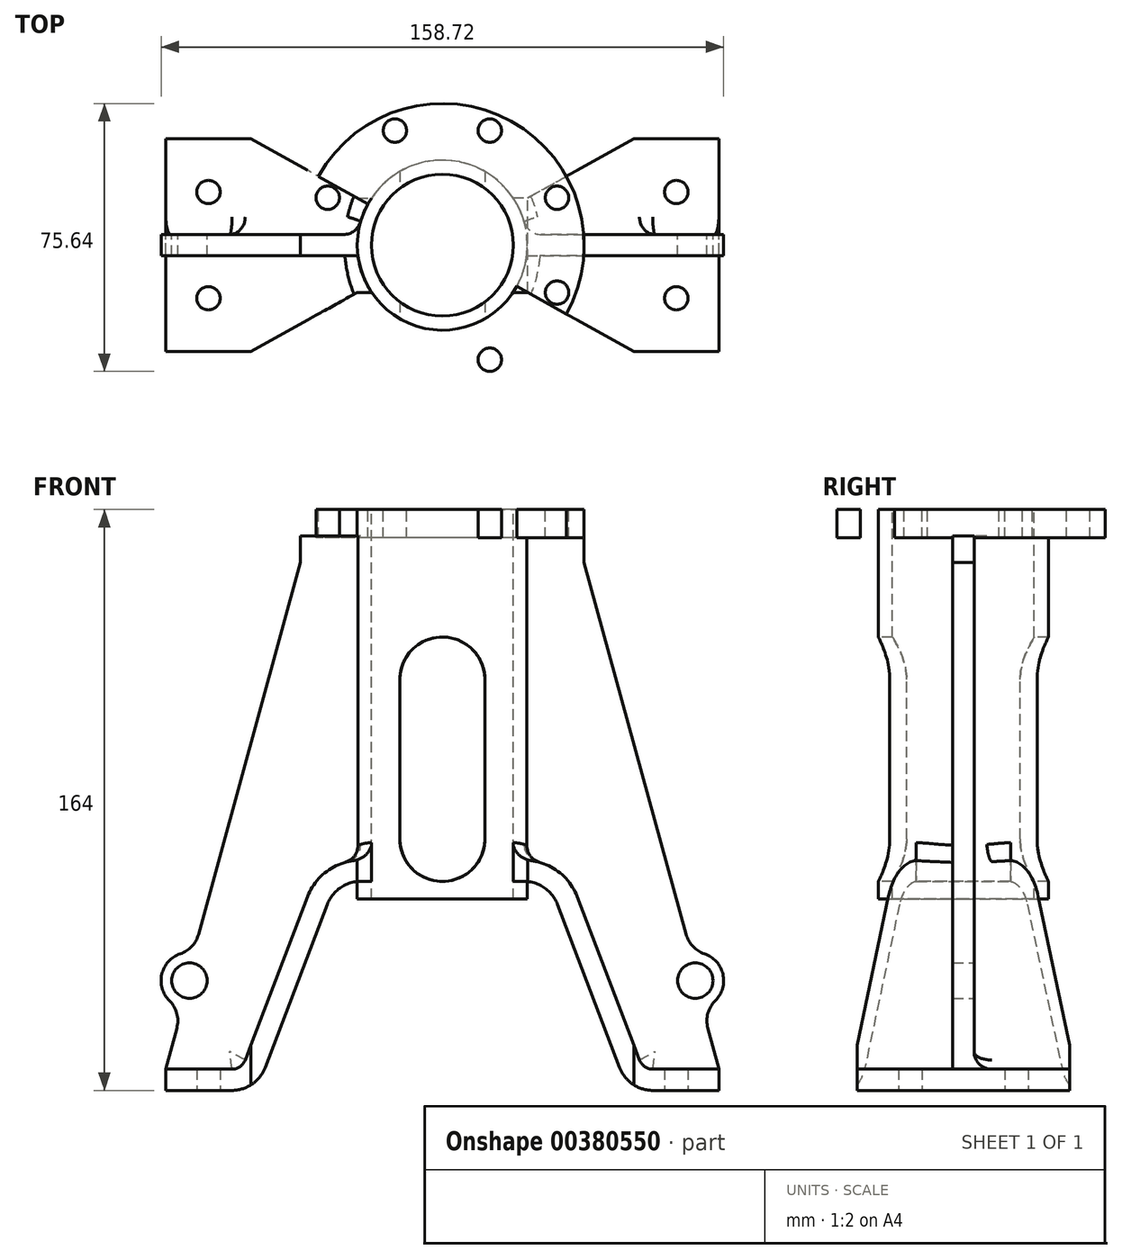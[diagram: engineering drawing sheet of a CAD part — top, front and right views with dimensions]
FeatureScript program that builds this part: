
annotation { "Feature Type Name" : "Feature", "Feature Type Description" : "" }
export const myFeature = defineFeature(function(context is Context, id is Id, definition is map)
    precondition{}
    {
        {
            var Q0;
            Q0=qCreatedBy(makeId("Top.planeOp"),FACE);
            var sketch = newSketch(context, id + "F0", { "sketchPlane" : qUnion([Q0])});
            skLineSegment(sketch, "E0", {"start": v(0, 47.18) * mm, "end": v(0, -47.18) * mm, "construction": true});
            skCircle(sketch, "E1", {"center": v(0, 0) * mm, "radius": 40 * mm});
            skLineSegment(sketch, "E2", {"start": v(-78, 0) * mm, "end": v(78, 0) * mm, "construction": true});
            skLineSegment(sketch, "E3.bottom", {"start": v(78, -3) * mm, "end": v(39.89, -3) * mm});
            skLineSegment(sketch, "E3.top", {"start": v(78, 3) * mm, "end": v(39.89, 3) * mm});
            skLineSegment(sketch, "E3.left", {"start": v(78, -3) * mm, "end": v(78, 3) * mm});
            skLineSegment(sketch, "E3.right", {"start": v(-78, -3) * mm, "end": v(-78, 3) * mm});
            skLineSegment(sketch, "E4.trimOffspring", {"start": v(-39.89, 3) * mm, "end": v(-78, 3) * mm});
            skLineSegment(sketch, "E5.trimOffspring", {"start": v(-39.89, -3) * mm, "end": v(-78, -3) * mm});
            skLineSegment(sketch, "E6", {"start": v(9.18, 22.17) * mm, "end": v(23.37, 56.42) * mm, "construction": true});
            skLineSegment(sketch, "E7", {"start": v(22.17, 9.18) * mm, "end": v(61.04, 25.28) * mm, "construction": true});
            skCircle(sketch, "E8", {"center": v(0, 0) * mm, "radius": 35 * mm, "construction": true});
            skCircle(sketch, "E9", {"center": v(13.4, 32.34) * mm, "radius": 3.3 * mm});
            skCircle(sketch, "E10", {"center": v(32.34, 13.4) * mm, "radius": 3.3 * mm});
            skLineSegment(sketch, "E11", {"start": v(78, -30) * mm, "end": v(78, 30) * mm});
            skLineSegment(sketch, "E12", {"start": v(78, 30) * mm, "end": v(54, 30) * mm});
            skLineSegment(sketch, "E13", {"start": v(20.98, 11.66) * mm, "end": v(54, 30) * mm});
            skCircle(sketch, "E14", {"center": v(66, 15) * mm, "radius": 3.3 * mm});
            skCircle(sketch, "E15.MirrorC", {"center": v(66, -15) * mm, "radius": 3.3 * mm});
            skLineSegment(sketch, "E16.MirrorCS", {"start": v(78, -30) * mm, "end": v(54, -30) * mm});
            skLineSegment(sketch, "E17.MirrorCS", {"start": v(20.98, -11.66) * mm, "end": v(54, -30) * mm});
            skCircle(sketch, "E18.MirrorC", {"center": v(32.34, -13.4) * mm, "radius": 3.3 * mm});
            skCircle(sketch, "E19.MirrorC", {"center": v(13.4, -32.34) * mm, "radius": 3.3 * mm});
            skLineSegment(sketch, "E20", {"start": v(66, 15) * mm, "end": v(66, 30) * mm, "construction": true});
            skLineSegment(sketch, "E21", {"start": v(66, 15) * mm, "end": v(78, 15) * mm, "construction": true});
            skCircle(sketch, "E22.MirrorC", {"center": v(-13.4, 32.34) * mm, "radius": 3.3 * mm});
            skCircle(sketch, "E23.MirrorC", {"center": v(-32.34, 13.4) * mm, "radius": 3.3 * mm});
            skCircle(sketch, "E24.MirrorC", {"center": v(-32.34, -13.4) * mm, "radius": 3.3 * mm});
            skCircle(sketch, "E25.MirrorC", {"center": v(-13.4, -32.34) * mm, "radius": 3.3 * mm});
            skCircle(sketch, "E26.MirrorC", {"center": v(-66, -15) * mm, "radius": 3.3 * mm});
            skLineSegment(sketch, "E27.MirrorCS", {"start": v(-78, -30) * mm, "end": v(-54, -30) * mm});
            skLineSegment(sketch, "E28.MirrorCS", {"start": v(-78, -30) * mm, "end": v(-78, 30) * mm});
            skLineSegment(sketch, "E29.MirrorCS", {"start": v(-78, 30) * mm, "end": v(-54, 30) * mm});
            skLineSegment(sketch, "E30.MirrorCS", {"start": v(-20.98, 11.66) * mm, "end": v(-54, 30) * mm});
            skLineSegment(sketch, "E31.MirrorCS", {"start": v(-20.98, -11.66) * mm, "end": v(-54, -30) * mm});
            skCircle(sketch, "E32.MirrorC", {"center": v(-66, 15) * mm, "radius": 3.3 * mm});
            skCircle(sketch, "E33", {"center": v(0, 0) * mm, "radius": 24 * mm});
            skCircle(sketch, "E34", {"center": v(0, 0) * mm, "radius": 20 * mm});
            skSolve(sketch);
        }
        {
            var Q0;
            Q0=makeQuery(id+"F0.imprint","IMPRINT",FACE,{"disambiguationData":[TD([[makeQuery(id+"F0.imprint","IMPRINT",EDGE,{"derivedFrom":sQuery(id+"F0.wireOp",EDGE,"E9")}),-1.0]])]});
            var Q1;
            Q1=makeQuery(id+"F0.imprint","IMPRINT",FACE,{"disambiguationData":[TD([[makeQuery(id+"F0.imprint","IMPRINT",EDGE,{"derivedFrom":sQuery(id+"F0.wireOp",EDGE,"E23.MirrorC")}),1.0]])]});
            var Q2;
            Q2=makeQuery(id+"F0.imprint","IMPRINT",FACE,{"disambiguationData":[TD([[makeQuery(id+"F0.imprint","IMPRINT",EDGE,{"derivedFrom":sQuery(id+"F0.wireOp",EDGE,"E19.MirrorC")}),1.0]])]});
            var Q3;
            Q3=makeQuery(id+"F0.imprint","IMPRINT",FACE,{"disambiguationData":[TD([[makeQuery(id+"F0.imprint","IMPRINT",EDGE,{"derivedFrom":sQuery(id+"F0.wireOp",EDGE,"E10")}),-1.0]])]});
            extrude(context, id + "F1", {"entities" : qUnion([Q0, Q1, Q2, Q3]), "oppositeDirection" : true, "depth" : 8 * mm});
        }
        {
            var Q0;
            Q0=qCreatedBy(makeId("Front.planeOp"),FACE);
            var sketch = newSketch(context, id + "F2", { "sketchPlane" : qUnion([Q0])});
            skLineSegment(sketch, "E35", {"start": v(40, 0) * mm, "end": v(40, -15) * mm});
            skLineSegment(sketch, "E36", {"start": v(0, 0) * mm, "end": v(0, -164) * mm, "construction": true});
            skLineSegment(sketch, "E37", {"start": v(59.35, -164) * mm, "end": v(78, -164) * mm});
            skLineSegment(sketch, "E38", {"start": v(78, -164) * mm, "end": v(78, -158) * mm});
            skLineSegment(sketch, "E39", {"start": v(78, -158) * mm, "end": v(74.92, -146.4) * mm});
            skLineSegment(sketch, "E40.bottom", {"start": v(-20, 0) * mm, "end": v(20, 0) * mm});
            skLineSegment(sketch, "E40.top", {"start": v(-20, -70.5) * mm, "end": v(20, -70.5) * mm, "construction": true});
            skLineSegment(sketch, "E40.left", {"start": v(-20, 0) * mm, "end": v(-20, -70.5) * mm, "construction": true});
            skLineSegment(sketch, "E40.right", {"start": v(20, 0) * mm, "end": v(20, -70.5) * mm, "construction": true});
            skCircle(sketch, "E41", {"center": v(0, -48) * mm, "radius": 12 * mm, "construction": true});
            skCircle(sketch, "E42", {"center": v(0, -93) * mm, "radius": 12 * mm, "construction": true});
            skPoint(sketch, "E43", {"position": v(0, -70.5) * mm});
            skLineSegment(sketch, "E44", {"start": v(0, -93) * mm, "end": v(-12, -93) * mm, "construction": true});
            skLineSegment(sketch, "E45", {"start": v(-12, -93) * mm, "end": v(-12, -48) * mm});
            skLineSegment(sketch, "E46", {"start": v(-12, -48) * mm, "end": v(12, -48) * mm, "construction": true});
            skLineSegment(sketch, "E47", {"start": v(12, -48) * mm, "end": v(12, -93) * mm});
            skLineSegment(sketch, "E48", {"start": v(12, -93) * mm, "end": v(-12, -93) * mm, "construction": true});
            skArc(sketch, "E49", {"start": v(12, -48) * mm, "mid": v(0, -36) * mm, "end": v(-12, -48) * mm});
            skArc(sketch, "E50", {"start": v(-12, -93) * mm, "mid": v(0, -105) * mm, "end": v(12, -93) * mm});
            skLineSegment(sketch, "E51", {"start": v(20, -70.5) * mm, "end": v(20, -112.54) * mm, "construction": true});
            skLineSegment(sketch, "E52", {"start": v(-20, -112.54) * mm, "end": v(-20, -70.5) * mm, "construction": true});
            skLineSegment(sketch, "E53", {"start": v(0, -105) * mm, "end": v(23.1, -105) * mm, "construction": true});
            skLineSegment(sketch, "E54", {"start": v(30, -105) * mm, "end": v(30, -164) * mm});
            skLineSegment(sketch, "E55", {"start": v(50, -157.56) * mm, "end": v(32.45, -111.44) * mm});
            skLineSegment(sketch, "E56", {"start": v(38.06, -109.3) * mm, "end": v(55.61, -155.42) * mm});
            skLineSegment(sketch, "E57", {"start": v(59.35, -158) * mm, "end": v(78, -158) * mm});
            skPoint(sketch, "E58.visualSharp", {"position": v(30, -105) * mm});
            skArc(sketch, "E58.filletArc", {"start": v(32.45, -111.44) * mm, "mid": v(28.78, -106.77) * mm, "end": v(23.1, -105) * mm});
            skPoint(sketch, "E59.newPointB", {"position": v(-78, -164) * mm});
            skArc(sketch, "E59.filletArc", {"start": v(50, -157.56) * mm, "mid": v(53.67, -162.23) * mm, "end": v(59.35, -164) * mm});
            skPoint(sketch, "E60.visualSharp", {"position": v(33.98, -98.59) * mm});
            skArc(sketch, "E60.filletArc", {"start": v(38.06, -109.3) * mm, "mid": v(32.19, -101.83) * mm, "end": v(23.1, -99) * mm});
            skPoint(sketch, "E61.visualSharp", {"position": v(56.6, -158) * mm});
            skArc(sketch, "E61.filletArc", {"start": v(55.61, -155.42) * mm, "mid": v(57.08, -157.3) * mm, "end": v(59.35, -158) * mm});
            skLineSegment(sketch, "E62.MirrorCS", {"start": v(-50, -157.56) * mm, "end": v(-32.45, -111.44) * mm});
            skLineSegment(sketch, "E63.MirrorCS", {"start": v(-38.06, -109.3) * mm, "end": v(-55.61, -155.42) * mm});
            skArc(sketch, "E64.MirrorCS", {"start": v(-38.06, -109.3) * mm, "mid": v(-32.19, -101.83) * mm, "end": v(-23.1, -99) * mm});
            skArc(sketch, "E65.MirrorCS", {"start": v(-32.45, -111.44) * mm, "mid": v(-28.78, -106.77) * mm, "end": v(-23.1, -105) * mm});
            skLineSegment(sketch, "E66.MirrorCS", {"start": v(-59.35, -158) * mm, "end": v(-78, -158) * mm});
            skArc(sketch, "E67.MirrorCS", {"start": v(-50, -157.56) * mm, "mid": v(-53.67, -162.23) * mm, "end": v(-59.35, -164) * mm});
            skPoint(sketch, "E68.MirrorP", {"position": v(-56.6, -158) * mm});
            skArc(sketch, "E69.MirrorCS", {"start": v(-55.61, -155.42) * mm, "mid": v(-57.08, -157.3) * mm, "end": v(-59.35, -158) * mm});
            skLineSegment(sketch, "E70.MirrorCS", {"start": v(-59.35, -164) * mm, "end": v(-78, -164) * mm});
            skLineSegment(sketch, "E71.MirrorCS", {"start": v(-78, -164) * mm, "end": v(-78, -158) * mm});
            skLineSegment(sketch, "E72.MirrorCS", {"start": v(-40, 0) * mm, "end": v(-40, -15) * mm});
            skLineSegment(sketch, "E73", {"start": v(-23.1, -99) * mm, "end": v(23.1, -99) * mm, "construction": true});
            skLineSegment(sketch, "E74", {"start": v(-23.1, -105) * mm, "end": v(23.1, -105) * mm, "construction": true});
            skCircle(sketch, "E75", {"center": v(71.36, -133) * mm, "radius": 5 * mm});
            skArc(sketch, "E76", {"start": v(77, -138.67) * mm, "mid": v(79.15, -131.2) * mm, "end": v(73.94, -125.43) * mm});
            skLineSegment(sketch, "E77", {"start": v(68.82, -119.98) * mm, "end": v(40, -15) * mm});
            skPoint(sketch, "E78.newPointB", {"position": v(40, -15) * mm});
            skArc(sketch, "E78.filletArc", {"start": v(77, -138.67) * mm, "mid": v(74.92, -142.25) * mm, "end": v(74.92, -146.4) * mm});
            skArc(sketch, "E79.filletArc", {"start": v(68.82, -119.98) * mm, "mid": v(70.7, -123.34) * mm, "end": v(73.94, -125.43) * mm});
            skLineSegment(sketch, "E80.MirrorCS", {"start": v(-68.82, -119.98) * mm, "end": v(-40, -15) * mm});
            skCircle(sketch, "E81.MirrorC", {"center": v(-71.36, -133) * mm, "radius": 5 * mm});
            skArc(sketch, "E82.MirrorCS", {"start": v(-77, -138.67) * mm, "mid": v(-79.15, -131.2) * mm, "end": v(-73.94, -125.43) * mm});
            skArc(sketch, "E83.MirrorCS", {"start": v(-77, -138.67) * mm, "mid": v(-74.92, -142.25) * mm, "end": v(-74.92, -146.4) * mm});
            skArc(sketch, "E84.MirrorCS", {"start": v(-68.82, -119.98) * mm, "mid": v(-70.7, -123.34) * mm, "end": v(-73.94, -125.43) * mm});
            skLineSegment(sketch, "E85.MirrorCS", {"start": v(-78, -158) * mm, "end": v(-74.92, -146.4) * mm});
            skLineSegment(sketch, "E86", {"start": v(-40, -7.5) * mm, "end": v(40, -7.5) * mm});
            skLineSegment(sketch, "E87.bottom", {"start": v(-24.01, 0) * mm, "end": v(24.02, 0) * mm});
            skLineSegment(sketch, "E87.top", {"start": v(-24.01, -112.5) * mm, "end": v(24.02, -112.5) * mm});
            skLineSegment(sketch, "E87.left", {"start": v(-24.01, 0) * mm, "end": v(-24.01, -112.5) * mm});
            skLineSegment(sketch, "E87.right", {"start": v(24.02, 0) * mm, "end": v(24.02, -112.5) * mm});
            skSolve(sketch);
        }
        {
            var Q0;
            Q0=makeQuery(id+"F0.imprint","IMPRINT",FACE,{"disambiguationData":[TD([[makeQuery(id+"F0.imprint","IMPRINT",EDGE,{"derivedFrom":sQuery(id+"F0.wireOp",EDGE,"E33")}),1.0]])]});
            extrude(context, id + "F3", {"entities" : qUnion([Q0]), "operationType" : NewBodyOperationType.ADD, "oppositeDirection" : true, "depth" : 110 * mm});
        }
        {
            var Q0;
            Q0=makeQuery(id+"F2.imprint","IMPRINT",FACE,{"disambiguationData":[TD([[makeQuery(id+"F2.imprint","IMPRINT",EDGE,{"derivedFrom":sQuery(id+"F2.wireOp",EDGE,"E45")}),-1.0]])]});
            extrude(context, id + "F4", {"entities" : qUnion([Q0]), "operationType" : NewBodyOperationType.REMOVE, "oppositeDirection" : true, "depth" : 61.5 * mm, "hasSecondDirection" : true, "secondDirectionOppositeDirection" : false, "secondDirectionDepth" : 75.8 * mm});
        }
        {
            var Q0;
            {var subQ4=sQuery(id+"F2.wireOp",EDGE,"E63.MirrorCS");Q0=makeQuery(id+"F2.imprint","IMPRINT",FACE,{"disambiguationData":[TD([[makeQuery(id+"F2.imprint","IMPRINT",EDGE,{"derivedFrom":subQ4}),-1.0]])]});}
            var Q1;
            Q1=makeQuery(id+"F2.imprint","IMPRINT",FACE,{"disambiguationData":[TD([[makeQuery(id+"F2.imprint","IMPRINT",EDGE,{"derivedFrom":sQuery(id+"F2.wireOp",EDGE,"E39")}),1.0]])]});
            extrude(context, id + "F5", {"entities" : qUnion([Q0, Q1]), "operationType" : NewBodyOperationType.ADD, "depth" : 3 * mm, "hasSecondDirection" : true, "secondDirectionOppositeDirection" : true, "secondDirectionDepth" : 3 * mm});
        }
        {
            var Q0;
            {var subQ1=sQuery(id+"F2.wireOp",EDGE,"E62.MirrorCS");Q0=makeQuery(id+"F2.imprint","IMPRINT",FACE,{"disambiguationData":[TD([[makeQuery(id+"F2.imprint","IMPRINT",EDGE,{"derivedFrom":subQ1}),1.0]])]});}
            var Q1;
            Q1=makeQuery(id+"F2.imprint","IMPRINT",FACE,{"disambiguationData":[TD([[makeQuery(id+"F2.imprint","IMPRINT",EDGE,{"derivedFrom":sQuery(id+"F2.wireOp",EDGE,"E37")}),1.0]])]});
            extrude(context, id + "F6", {"entities" : qUnion([Q0, Q1]), "operationType" : NewBodyOperationType.ADD, "depth" : 30 * mm, "hasSecondDirection" : true, "secondDirectionOppositeDirection" : true, "secondDirectionDepth" : 30 * mm});
        }
        {
            var Q0;
            {var subQ0=sQuery(id+"F2.wireOp",EDGE,"E69.MirrorCS");var subQ1=sQuery(id+"F2.wireOp",EDGE,"E87.left");var subQ2=sQuery(id+"F2.wireOp",EDGE,"E71.MirrorCS");var subQ3=sQuery(id+"F2.wireOp",EDGE,"E66.MirrorCS");var subQ4=sQuery(id+"F2.wireOp",EDGE,"E64.MirrorCS");var subQ5=sQuery(id+"F2.wireOp",EDGE,"E63.MirrorCS");Q0=makeQuery(id+"F6.boolean.opBoolean","SPLIT",FACE,{"disambiguationData":[TD([makeQuery(id+"F6.opExtrude","CAP_FACE",FACE,{"disambiguationData":[OSD([sQuery(id+"F2.wireOp",EDGE,"E62.MirrorCS"),subQ5,subQ4,sQuery(id+"F2.wireOp",EDGE,"E65.MirrorCS"),subQ3,sQuery(id+"F2.wireOp",EDGE,"E67.MirrorCS"),subQ0,sQuery(id+"F2.wireOp",EDGE,"E70.MirrorCS"),subQ2,subQ1])],"isStart":false})])],"derivedFrom":makeQuery(id+"F6.opExtrude","SWEPT_FACE",FACE,{"disambiguationData":[OSD([subQ3])]})});}
            var sketch = newSketch(context, id + "F7", { "sketchPlane" : qUnion([Q0])});
            skLineSegment(sketch, "E88.0", {"start": v(-20.98, -11.66) * mm, "end": v(-54, -30) * mm});
            skLineSegment(sketch, "E89", {"start": v(-54, -30) * mm, "end": v(-20.98, -30) * mm});
            skLineSegment(sketch, "E90", {"start": v(-20.98, -30) * mm, "end": v(-20.98, -11.66) * mm});
            skLineSegment(sketch, "E91.MirrorCS", {"start": v(20.98, -30) * mm, "end": v(20.98, -11.66) * mm});
            skLineSegment(sketch, "E92.MirrorCS", {"start": v(54, -30) * mm, "end": v(20.98, -30) * mm});
            skLineSegment(sketch, "E93.MirrorCS", {"start": v(20.98, -11.66) * mm, "end": v(54, -30) * mm});
            skLineSegment(sketch, "E94.MirrorCS", {"start": v(54, 30) * mm, "end": v(20.98, 30) * mm});
            skLineSegment(sketch, "E95.MirrorCS", {"start": v(20.98, 11.66) * mm, "end": v(54, 30) * mm});
            skLineSegment(sketch, "E96.MirrorCS", {"start": v(20.98, 30) * mm, "end": v(20.98, 11.66) * mm});
            skLineSegment(sketch, "E97.MirrorCS", {"start": v(-20.98, 30) * mm, "end": v(-20.98, 11.66) * mm});
            skLineSegment(sketch, "E98.MirrorCS", {"start": v(-54, 30) * mm, "end": v(-20.98, 30) * mm});
            skLineSegment(sketch, "E99.MirrorCS", {"start": v(-20.98, 11.66) * mm, "end": v(-54, 30) * mm});
            skCircle(sketch, "E100.0", {"center": v(-66, 15) * mm, "radius": 3.3 * mm});
            skCircle(sketch, "E101.0", {"center": v(66, 15) * mm, "radius": 3.3 * mm});
            skCircle(sketch, "E102.0", {"center": v(66, -15) * mm, "radius": 3.3 * mm});
            skCircle(sketch, "E103.0", {"center": v(-66, -15) * mm, "radius": 3.3 * mm});
            skSolve(sketch);
        }
        {
            var Q0;
            Q0=qSketchRegion(id+"F7",true);
            var Q1;
            Q1=makeQuery(id+"F6.opExtrude","CAP_VERTEX",VERTEX,{"disambiguationData":[OSD([sQuery(id+"F2.wireOp",EDGE,"E64.MirrorCS"),sQuery(id+"F2.wireOp",EDGE,"E87.left")])],"isStart":false});
            extrude(context, id + "F8", {"entities" : qUnion([Q0]), "operationType" : NewBodyOperationType.REMOVE, "endBound" : BoundingType.UP_TO_VERTEX, "endBoundEntityVertex" : qUnion([Q1]), "depth" : 25 * mm, "hasSecondDirection" : true, "secondDirectionOppositeDirection" : true, "secondDirectionDepth" : 40.5 * mm});
        }
        {
            var Q0;
            {var subQ0=sQuery(id+"F2.wireOp",EDGE,"E87.right");Q0=makeQuery(id+"F6.boolean.opBoolean","MERGE",FACE,{"derivedFrom":[makeQuery(id+"F5.opExtrude","SWEPT_FACE",FACE,{"disambiguationData":[OSD([subQ0])]}),makeQuery(id+"F6.opExtrude","SWEPT_FACE",FACE,{"disambiguationData":[OSD([subQ0])]})]});}
            extrude(context, id + "F9", {"entities" : qUnion([Q0]), "operationType" : NewBodyOperationType.ADD, "depth" : 25 * mm});
        }
        {
            var Q0;
            {var subQ0=sQuery(id+"F2.wireOp",EDGE,"E87.left");Q0=makeQuery(id+"F6.boolean.opBoolean","MERGE",FACE,{"derivedFrom":[makeQuery(id+"F5.opExtrude","SWEPT_FACE",FACE,{"disambiguationData":[OSD([subQ0])]}),makeQuery(id+"F6.opExtrude","SWEPT_FACE",FACE,{"disambiguationData":[OSD([subQ0])]})]});}
            extrude(context, id + "F10", {"entities" : qUnion([Q0]), "operationType" : NewBodyOperationType.ADD, "depth" : 25 * mm});
        }
        {
            var Q0;
            Q0=makeQuery(id+"F0.imprint","IMPRINT",FACE,{"disambiguationData":[TD([[makeQuery(id+"F0.imprint","IMPRINT",EDGE,{"derivedFrom":sQuery(id+"F0.wireOp",EDGE,"E34")}),1.0]])]});
            extrude(context, id + "F11", {"entities" : qUnion([Q0]), "operationType" : NewBodyOperationType.REMOVE, "oppositeDirection" : true, "depth" : 621.2 * mm});
        }
        {
            var Q0;
            {var subQ0=sQuery(id+"F2.wireOp",EDGE,"E87.right");var subQ1=sQuery(id+"F2.wireOp",EDGE,"E61.filletArc");var subQ2=sQuery(id+"F2.wireOp",EDGE,"E60.filletArc");var subQ3=sQuery(id+"F2.wireOp",EDGE,"E57");var subQ4=sQuery(id+"F2.wireOp",EDGE,"E56");Q0=makeQuery(id+"F9.boolean.opBoolean","INTERSECT",EDGE,{"derivedFrom":[makeQuery(id+"F3.opExtrude","SWEPT_FACE",FACE,{"disambiguationData":[OSD([sQuery(id+"F0.wireOp",EDGE,"E33")])]}),makeQuery(id+"F9.opExtrude","SWEPT_FACE",FACE,{"disambiguationData":[OSD([subQ2,subQ0]),TDD([makeQuery(id+"F6.boolean.opBoolean","SPLIT",EDGE,{"disambiguationData":[TD([makeQuery(id+"F6.opExtrude","CAP_FACE",FACE,{"disambiguationData":[OSD([sQuery(id+"F2.wireOp",EDGE,"E37"),sQuery(id+"F2.wireOp",EDGE,"E38"),sQuery(id+"F2.wireOp",EDGE,"E55"),subQ4,subQ3,sQuery(id+"F2.wireOp",EDGE,"E58.filletArc"),sQuery(id+"F2.wireOp",EDGE,"E59.filletArc"),subQ2,subQ1,subQ0])],"isStart":true})])],"derivedFrom":makeQuery(id+"F6.opExtrude","SWEPT_EDGE",EDGE,{"disambiguationData":[OSD([subQ2,subQ0])]})})])]})]});}
            var Q1;
            {var subQ0=sQuery(id+"F2.wireOp",EDGE,"E60.filletArc");var subQ1=sQuery(id+"F2.wireOp",EDGE,"E87.right");var subQ2=sQuery(id+"F2.wireOp",EDGE,"E61.filletArc");var subQ3=sQuery(id+"F2.wireOp",EDGE,"E57");var subQ4=sQuery(id+"F2.wireOp",EDGE,"E56");Q1=makeQuery(id+"F9.boolean.opBoolean","INTERSECT",EDGE,{"derivedFrom":[makeQuery(id+"F3.opExtrude","SWEPT_FACE",FACE,{"disambiguationData":[OSD([sQuery(id+"F0.wireOp",EDGE,"E33")])]}),makeQuery(id+"F9.opExtrude","SWEPT_FACE",FACE,{"disambiguationData":[OSD([subQ0,subQ1]),TDD([makeQuery(id+"F6.boolean.opBoolean","SPLIT",EDGE,{"disambiguationData":[TD([makeQuery(id+"F6.opExtrude","CAP_FACE",FACE,{"disambiguationData":[OSD([sQuery(id+"F2.wireOp",EDGE,"E37"),sQuery(id+"F2.wireOp",EDGE,"E38"),sQuery(id+"F2.wireOp",EDGE,"E55"),subQ4,subQ3,sQuery(id+"F2.wireOp",EDGE,"E58.filletArc"),sQuery(id+"F2.wireOp",EDGE,"E59.filletArc"),subQ0,subQ2,subQ1])],"isStart":false})])],"derivedFrom":makeQuery(id+"F6.opExtrude","SWEPT_EDGE",EDGE,{"disambiguationData":[OSD([subQ0,subQ1])]})})])]})]});}
            var Q2;
            {var subQ0=sQuery(id+"F2.wireOp",EDGE,"E64.MirrorCS");var subQ1=sQuery(id+"F2.wireOp",EDGE,"E87.left");var subQ2=sQuery(id+"F2.wireOp",EDGE,"E69.MirrorCS");var subQ3=sQuery(id+"F2.wireOp",EDGE,"E66.MirrorCS");var subQ4=sQuery(id+"F2.wireOp",EDGE,"E63.MirrorCS");Q2=makeQuery(id+"F10.boolean.opBoolean","INTERSECT",EDGE,{"derivedFrom":[makeQuery(id+"F3.opExtrude","SWEPT_FACE",FACE,{"disambiguationData":[OSD([sQuery(id+"F0.wireOp",EDGE,"E33")])]}),makeQuery(id+"F10.opExtrude","SWEPT_FACE",FACE,{"disambiguationData":[OSD([subQ0,subQ1]),TDD([makeQuery(id+"F6.boolean.opBoolean","SPLIT",EDGE,{"disambiguationData":[TD([makeQuery(id+"F6.opExtrude","CAP_FACE",FACE,{"disambiguationData":[OSD([sQuery(id+"F2.wireOp",EDGE,"E62.MirrorCS"),subQ4,subQ0,sQuery(id+"F2.wireOp",EDGE,"E65.MirrorCS"),subQ3,sQuery(id+"F2.wireOp",EDGE,"E67.MirrorCS"),subQ2,sQuery(id+"F2.wireOp",EDGE,"E70.MirrorCS"),sQuery(id+"F2.wireOp",EDGE,"E71.MirrorCS"),subQ1])],"isStart":true})])],"derivedFrom":makeQuery(id+"F6.opExtrude","SWEPT_EDGE",EDGE,{"disambiguationData":[OSD([subQ0,subQ1])]})})])]})]});}
            var Q3;
            {var subQ0=sQuery(id+"F2.wireOp",EDGE,"E64.MirrorCS");var subQ1=sQuery(id+"F2.wireOp",EDGE,"E87.left");var subQ2=sQuery(id+"F2.wireOp",EDGE,"E69.MirrorCS");var subQ3=sQuery(id+"F2.wireOp",EDGE,"E66.MirrorCS");var subQ4=sQuery(id+"F2.wireOp",EDGE,"E63.MirrorCS");Q3=makeQuery(id+"F10.boolean.opBoolean","INTERSECT",EDGE,{"derivedFrom":[makeQuery(id+"F3.opExtrude","SWEPT_FACE",FACE,{"disambiguationData":[OSD([sQuery(id+"F0.wireOp",EDGE,"E33")])]}),makeQuery(id+"F10.opExtrude","SWEPT_FACE",FACE,{"disambiguationData":[OSD([subQ0,subQ1]),TDD([makeQuery(id+"F6.boolean.opBoolean","SPLIT",EDGE,{"disambiguationData":[TD([makeQuery(id+"F6.opExtrude","CAP_FACE",FACE,{"disambiguationData":[OSD([sQuery(id+"F2.wireOp",EDGE,"E62.MirrorCS"),subQ4,subQ0,sQuery(id+"F2.wireOp",EDGE,"E65.MirrorCS"),subQ3,sQuery(id+"F2.wireOp",EDGE,"E67.MirrorCS"),subQ2,sQuery(id+"F2.wireOp",EDGE,"E70.MirrorCS"),sQuery(id+"F2.wireOp",EDGE,"E71.MirrorCS"),subQ1])],"isStart":false})])],"derivedFrom":makeQuery(id+"F6.opExtrude","SWEPT_EDGE",EDGE,{"disambiguationData":[OSD([subQ0,subQ1])]})})])]})]});}
            fillet(context, id + "F12", {"entities" : qUnion([Q0, Q1, Q2, Q3]), "radius" : 5 * mm, "tangentPropagation" : true, "allowEdgeOverflow" : false});
        }
        {
            var Q0;
            Q0=makeQuery(id+"F5.opExtrude","CAP_EDGE",EDGE,{"disambiguationData":[OSD([sQuery(id+"F2.wireOp",EDGE,"E60.filletArc")])],"isStart":true});
            var Q1;
            Q1=makeQuery(id+"F5.opExtrude","CAP_EDGE",EDGE,{"disambiguationData":[OSD([sQuery(id+"F2.wireOp",EDGE,"E60.filletArc")])],"isStart":false});
            var Q2;
            Q2=makeQuery(id+"F5.opExtrude","CAP_EDGE",EDGE,{"disambiguationData":[OSD([sQuery(id+"F2.wireOp",EDGE,"E64.MirrorCS")])],"isStart":false});
            var Q3;
            Q3=makeQuery(id+"F5.opExtrude","CAP_EDGE",EDGE,{"disambiguationData":[OSD([sQuery(id+"F2.wireOp",EDGE,"E64.MirrorCS")])],"isStart":true});
            fillet(context, id + "F13", {"entities" : qUnion([Q0, Q1, Q2, Q3]), "radius" : 5 * mm, "tangentPropagation" : true, "allowEdgeOverflow" : false});
        }
    });
